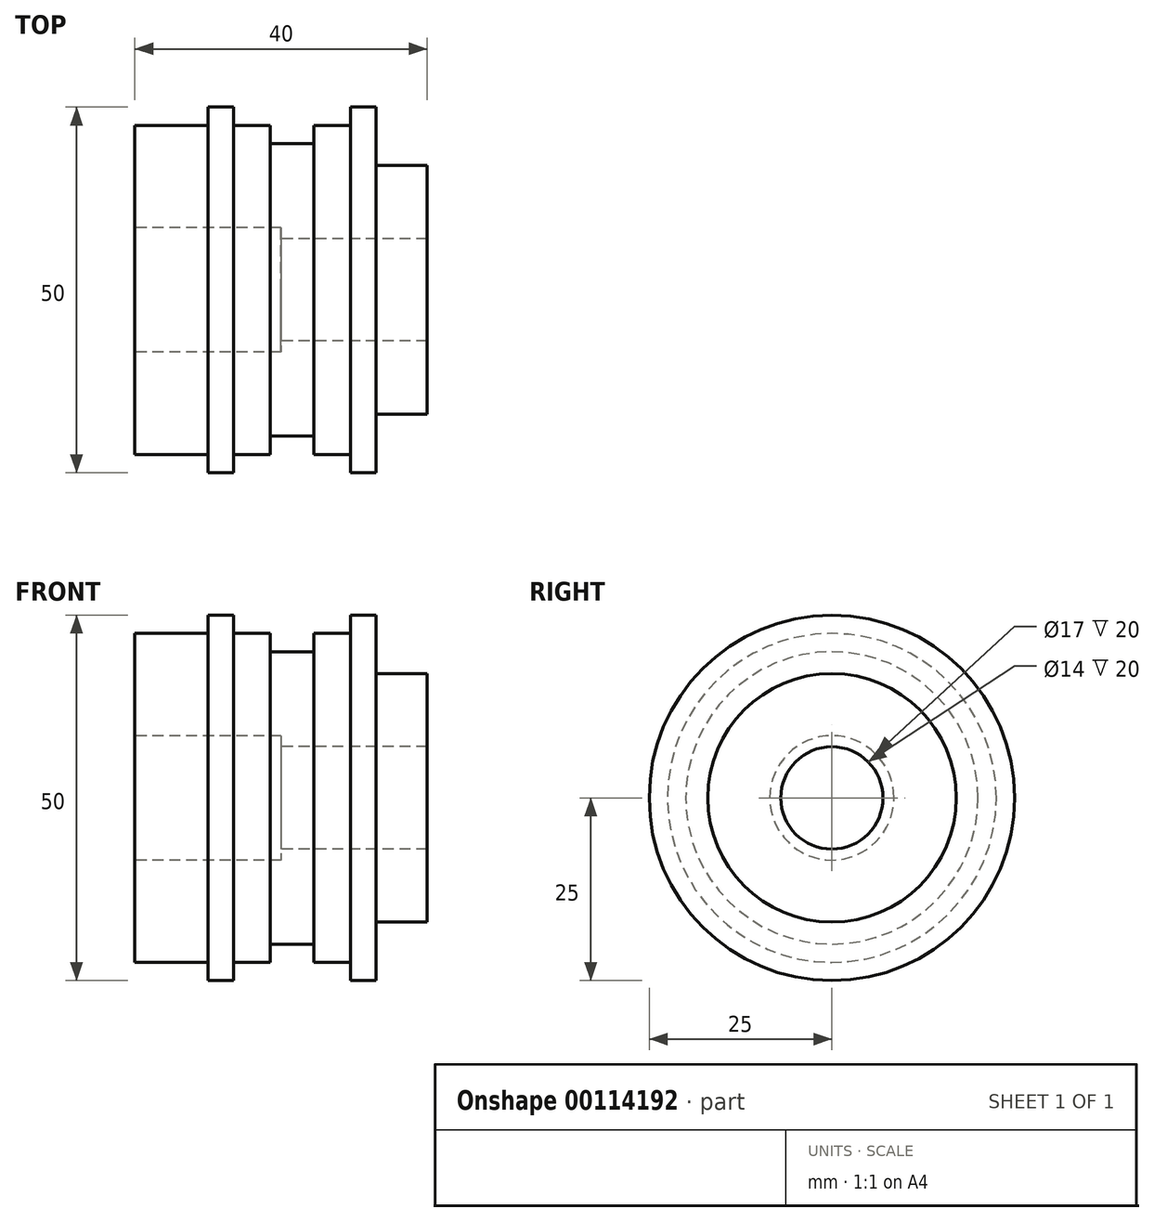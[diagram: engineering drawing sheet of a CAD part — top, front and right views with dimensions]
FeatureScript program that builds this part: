
annotation { "Feature Type Name" : "Feature", "Feature Type Description" : "" }
export const myFeature = defineFeature(function(context is Context, id is Id, definition is map)
    precondition{}
    {
        {
            var Q0;
            Q0=qCreatedBy(makeId("Front.planeOp"),FACE);
            var sketch = newSketch(context, id + "F0", { "sketchPlane" : qUnion([Q0])});
            skLineSegment(sketch, "E0", {"start": v(0, 0) * mm, "end": v(250.98, 0) * mm});
            skCircle(sketch, "E1", {"center": v(0, 0) * mm, "radius": 15 * mm});
            skCircle(sketch, "E2", {"center": v(0, 0) * mm, "radius": 27.5 * mm});
            skLineSegment(sketch, "E3", {"start": v(24.5, 12.5) * mm, "end": v(205, 12.5) * mm});
            skLineSegment(sketch, "E4", {"start": v(250, 8) * mm, "end": v(250, 0) * mm});
            skLineSegment(sketch, "E5", {"start": v(205, 12.5) * mm, "end": v(205, 8.5) * mm});
            skLineSegment(sketch, "E6", {"start": v(205, 8.5) * mm, "end": v(225, 8.5) * mm});
            skLineSegment(sketch, "E7", {"start": v(225, 8.5) * mm, "end": v(225, 8) * mm});
            skLineSegment(sketch, "E8", {"start": v(225, 8) * mm, "end": v(250, 8) * mm});
            skSolve(sketch);
        }
        {
            var Q0;
            Q0=qCreatedBy(makeId("Front.planeOp"),FACE);
            var sketch = newSketch(context, id + "F1", { "sketchPlane" : qUnion([Q0])});
            skLineSegment(sketch, "E9", {"start": v(54.7, 12.5) * mm, "end": v(54.7, 29) * mm});
            skLineSegment(sketch, "E10", {"start": v(54.7, 29) * mm, "end": v(60.7, 29) * mm});
            skLineSegment(sketch, "E11", {"start": v(60.7, 29) * mm, "end": v(60.7, 27.5) * mm});
            skLineSegment(sketch, "E12", {"start": v(60.7, 27.5) * mm, "end": v(76.24, 27.5) * mm});
            skLineSegment(sketch, "E13", {"start": v(76.24, 27.5) * mm, "end": v(79.7, 25.5) * mm});
            skLineSegment(sketch, "E14", {"start": v(79.7, 25.5) * mm, "end": v(94.7, 25.5) * mm});
            skLineSegment(sketch, "E15", {"start": v(94.7, 25.5) * mm, "end": v(94.7, 12.5) * mm});
            skLineSegment(sketch, "E16", {"start": v(94.7, 12.5) * mm, "end": v(54.7, 12.5) * mm});
            skLineSegment(sketch, "E17", {"start": v(66.7, 12.5) * mm, "end": v(66.7, 18) * mm});
            skLineSegment(sketch, "E18", {"start": v(66.7, 18) * mm, "end": v(76.7, 18) * mm});
            skLineSegment(sketch, "E19", {"start": v(76.7, 18) * mm, "end": v(76.7, 12.5) * mm});
            skLineSegment(sketch, "E20", {"start": v(54.7, 14) * mm, "end": v(56.7, 14) * mm});
            skLineSegment(sketch, "E21", {"start": v(56.7, 14) * mm, "end": v(56.7, 16) * mm});
            skLineSegment(sketch, "E22", {"start": v(56.7, 16) * mm, "end": v(60.7, 16) * mm});
            skLineSegment(sketch, "E23", {"start": v(60.7, 16) * mm, "end": v(60.7, 12.5) * mm});
            skLineSegment(sketch, "E24.bottom", {"start": v(85.7, 25.5) * mm, "end": v(89.7, 25.5) * mm});
            skLineSegment(sketch, "E24.top", {"start": v(85.7, 23.5) * mm, "end": v(89.7, 23.5) * mm});
            skLineSegment(sketch, "E24.left", {"start": v(85.7, 25.5) * mm, "end": v(85.7, 23.5) * mm});
            skLineSegment(sketch, "E24.right", {"start": v(89.7, 25.5) * mm, "end": v(89.7, 23.5) * mm});
            skLineSegment(sketch, "E25", {"start": v(48.25, 0) * mm, "end": v(103.65, 0) * mm});
            skSolve(sketch);
        }
        {
            var Q0;
            Q0=qCreatedBy(makeId("Front.planeOp"),FACE);
            var sketch = newSketch(context, id + "F2", { "sketchPlane" : qUnion([Q0])});
            skLineSegment(sketch, "E26", {"start": v(205, 22.5) * mm, "end": v(215, 22.5) * mm});
            skLineSegment(sketch, "E27", {"start": v(215, 22.5) * mm, "end": v(215, 25) * mm});
            skLineSegment(sketch, "E28", {"start": v(215, 25) * mm, "end": v(218.5, 25) * mm});
            skLineSegment(sketch, "E29", {"start": v(218.5, 25) * mm, "end": v(218.5, 22.5) * mm});
            skLineSegment(sketch, "E30", {"start": v(218.5, 22.5) * mm, "end": v(223.5, 22.5) * mm});
            skLineSegment(sketch, "E31", {"start": v(223.5, 22.5) * mm, "end": v(223.5, 20) * mm});
            skLineSegment(sketch, "E32", {"start": v(223.5, 20) * mm, "end": v(229.5, 20) * mm});
            skLineSegment(sketch, "E33", {"start": v(229.5, 20) * mm, "end": v(229.5, 22.5) * mm});
            skLineSegment(sketch, "E34", {"start": v(229.5, 22.5) * mm, "end": v(234.5, 22.5) * mm});
            skLineSegment(sketch, "E35", {"start": v(234.5, 22.5) * mm, "end": v(234.5, 25) * mm});
            skLineSegment(sketch, "E36", {"start": v(234.5, 25) * mm, "end": v(238, 25) * mm});
            skLineSegment(sketch, "E37", {"start": v(238, 25) * mm, "end": v(238, 17) * mm});
            skLineSegment(sketch, "E38", {"start": v(238, 17) * mm, "end": v(245, 17) * mm});
            skLineSegment(sketch, "E39", {"start": v(245, 17) * mm, "end": v(245, 7) * mm});
            skLineSegment(sketch, "E40", {"start": v(245, 7) * mm, "end": v(225, 7) * mm});
            skLineSegment(sketch, "E41", {"start": v(225, 7) * mm, "end": v(225, 8.5) * mm});
            skLineSegment(sketch, "E42", {"start": v(225, 8.5) * mm, "end": v(205, 8.5) * mm});
            skLineSegment(sketch, "E43", {"start": v(205, 8.5) * mm, "end": v(205, 22.5) * mm});
            skLineSegment(sketch, "E44", {"start": v(202.2, 0) * mm, "end": v(255.65, 0) * mm});
            skSolve(sketch);
        }
        {
            var Q0;
            Q0=makeQuery(id+"F2.imprint","IMPRINT",FACE,{"disambiguationData":[TD([[makeQuery(id+"F2.imprint","IMPRINT",EDGE,{"derivedFrom":sQuery(id+"F2.wireOp",EDGE,"E26")}),-1.0]])]});
            var Q1;
            Q1=sQuery(id+"F2.wireOp",EDGE,"E44");
            revolve(context, id + "F3", {"entities" : qUnion([Q0]), "axis" : qUnion([Q1]), "revolveType" : RevolveType.FULL});
        }
    });
